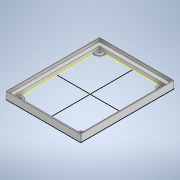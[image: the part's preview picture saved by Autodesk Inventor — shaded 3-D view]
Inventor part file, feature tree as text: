
AUTODESK INVENTOR PART (.ipt)
format: ipt  version: 2020 (Build 240168000, 168)  size: 354,816 bytes
history: native  units: mm
features: other x4, sketch x4, extrude x3, fillet x2
ambient origin geometry x8: Origin, YZ Plane, XZ Plane, XY Plane, X Axis, Y Axis, Z Axis, Center Point
bodies: Solid1 (feature_tree)
feature tree (13):
  other  "LCDScreen.ipt"
  extrude  "Extrusion1"  Depth=2.0mm
  extrude  "Extrusion3"  Depth=2.0mm
  fillet  "Fillet1"  Radius=2.0mm
  extrude  "Extrusion4"  Depth=25.0mm
  fillet  "Fillet2"  Radius=25.0mm
  sketch  "Sketch7"  dims[d29=25.0mm d30=25.0mm d31=25.0mm d32=25.0mm d33=25.0mm d34=25.0mm d35=3.5mm d36=0.0mm d37=20.0mm d38=4.0mm d39=10.0mm d40=4.0mm d41=10.0mm d42=4.0mm d43=10.0mm d44=2.0mm d45=2.0mm d46=2.0mm d47=2.0mm d48=3.0mm d49=0.0mm d50=2.0mm d56=16.5mm d57=15.5mm d74=10.0mm]
  other  "TaggingFeature1"
  sketch  "Sketch1"  dims[d0=10.0mm d1=2.0mm]
  sketch  "Sketch4"  dims[d2=2.0mm d3=2.0mm d4=2.0mm]
  sketch  "Sketch5"  dims[d5=10.0mm d6=0.0mm d27=25.0mm d28=25.0mm]
  other  "Solid1::LCDScreen.ipt"
  other  "Srf1"
